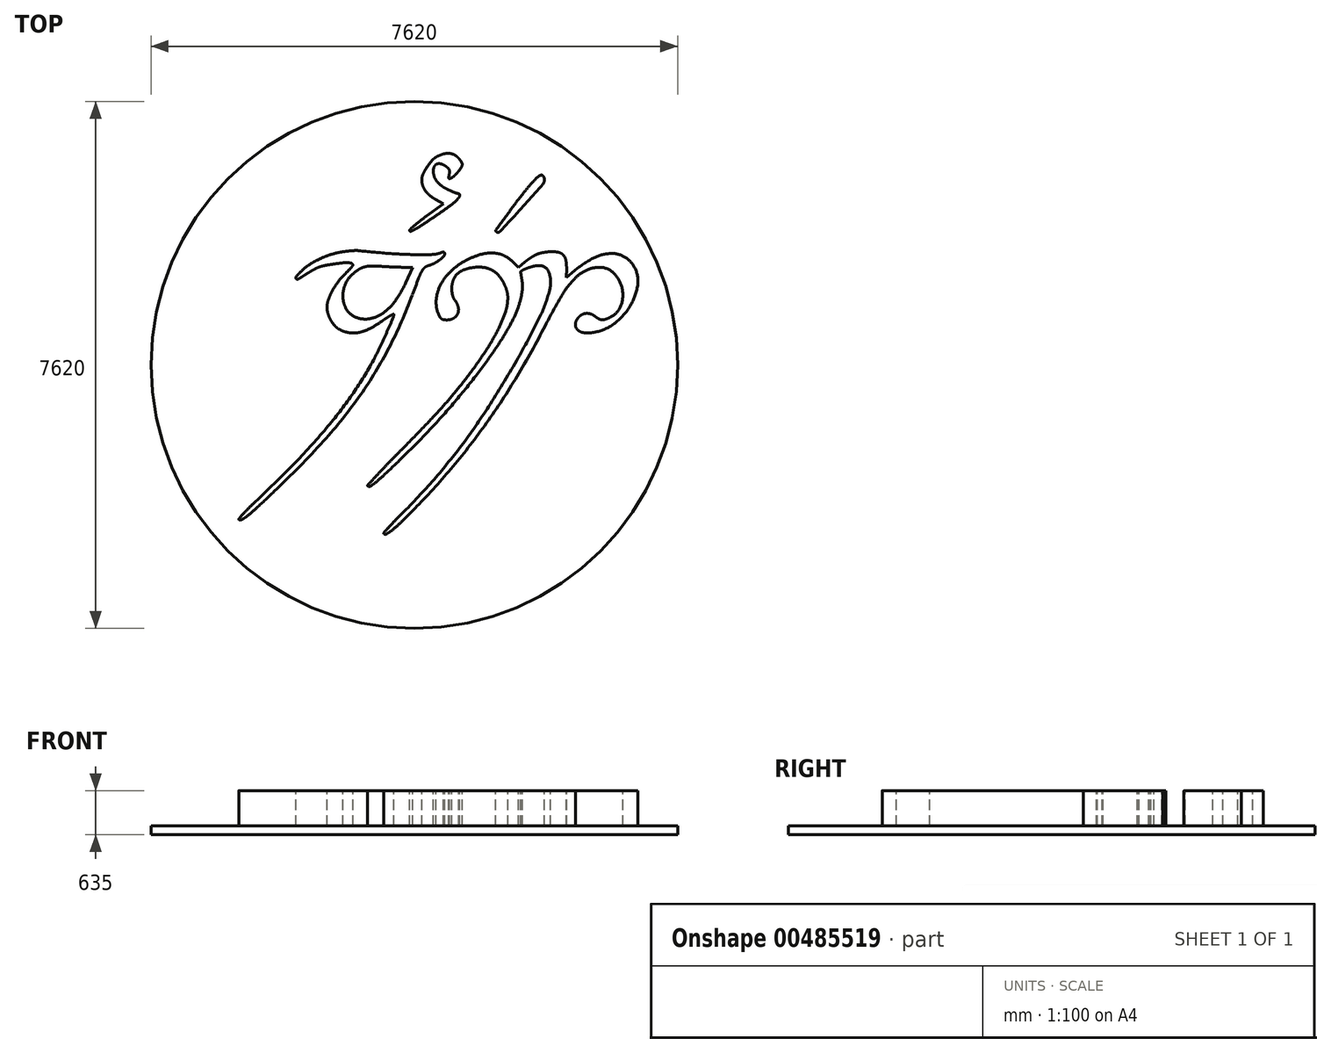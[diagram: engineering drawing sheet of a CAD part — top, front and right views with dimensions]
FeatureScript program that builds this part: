
annotation { "Feature Type Name" : "Feature", "Feature Type Description" : "" }
export const myFeature = defineFeature(function(context is Context, id is Id, definition is map)
    precondition{}
    {
        {
            var Q0;
            Q0=qCreatedBy(makeId("Top.planeOp"),FACE);
            var sketch = newSketch(context, id + "F0", { "sketchPlane" : qUnion([Q0])});
            skCircle(sketch, "E0", {"center": v(-347.42, -304.6) * mm, "radius": 3810 * mm});
            skSolve(sketch);
        }
        {
            var Q0;
            Q0=makeQuery(id+"F0.imprint","IMPRINT",FACE,{"disambiguationData":[TD([[makeQuery(id+"F0.imprint","IMPRINT",EDGE,{"derivedFrom":sQuery(id+"F0.wireOp",EDGE,"E0")}),1.0]])]});
            extrude(context, id + "F1", {"entities" : qUnion([Q0]), "depth" : 635 * mm});
        }
        {
            var Q0;
            Q0=makeQuery(id+"F1.opExtrude","CAP_FACE",FACE,{"disambiguationData":[OSD([sQuery(id+"F0.wireOp",EDGE,"E0")])],"isStart":false});
            var sketch = newSketch(context, id + "F2", { "sketchPlane" : qUnion([Q0])});
            skArc(sketch, "E1", {"start": v(-7.42, 2714.2) * mm, "mid": v(-48.53, 2689.23) * mm, "end": v(-84.64, 2657.45) * mm});
            skArc(sketch, "E2", {"start": v(-84.64, 2657.45) * mm, "mid": v(-125.21, 2611.05) * mm, "end": v(-161.69, 2561.37) * mm});
            skArc(sketch, "E3", {"start": v(-161.69, 2561.37) * mm, "mid": v(-193.23, 2509.73) * mm, "end": v(-220.26, 2455.6) * mm});
            skArc(sketch, "E4", {"start": v(-220.26, 2455.6) * mm, "mid": v(-234, 2413.5) * mm, "end": v(-238.66, 2369.44) * mm});
            skArc(sketch, "E5", {"start": v(-238.66, 2369.44) * mm, "mid": v(-235.35, 2329.08) * mm, "end": v(-225.53, 2289.8) * mm});
            skArc(sketch, "E6", {"start": v(-225.53, 2289.8) * mm, "mid": v(-209.14, 2250.91) * mm, "end": v(-187.32, 2214.8) * mm});
            skArc(sketch, "E7", {"start": v(-187.32, 2214.8) * mm, "mid": v(-158.36, 2179.04) * mm, "end": v(-125, 2147.33) * mm});
            skArc(sketch, "E8", {"start": v(-125, 2147.33) * mm, "mid": v(-84.35, 2116.63) * mm, "end": v(-40.94, 2089.97) * mm});
            skLineSegment(sketch, "E9", {"start": v(-40.94, 2089.97) * mm, "end": v(71.82, 2027.96) * mm});
            skLineSegment(sketch, "E10", {"start": v(71.82, 2027.96) * mm, "end": v(-172.32, 1846.85) * mm});
            skArc(sketch, "E11", {"start": v(-172.32, 1846.85) * mm, "mid": v(-219.33, 1811.5) * mm, "end": v(-265.89, 1775.55) * mm});
            skArc(sketch, "E12", {"start": v(-265.89, 1775.55) * mm, "mid": v(-305.63, 1743.8) * mm, "end": v(-344.74, 1711.28) * mm});
            skArc(sketch, "E13", {"start": v(-344.74, 1711.28) * mm, "mid": v(-377.18, 1683.48) * mm, "end": v(-409.36, 1655.37) * mm});
            skArc(sketch, "E14", {"start": v(-409.36, 1655.37) * mm, "mid": v(-414.6, 1648.27) * mm, "end": v(-416.46, 1639.65) * mm});
            skArc(sketch, "E15", {"start": v(-416.46, 1639.65) * mm, "mid": v(-410.61, 1628.75) * mm, "end": v(-398.3, 1627.6) * mm});
            skArc(sketch, "E16", {"start": v(-398.3, 1627.6) * mm, "mid": v(-361.58, 1644.42) * mm, "end": v(-325.94, 1663.42) * mm});
            skArc(sketch, "E17", {"start": v(-325.94, 1663.42) * mm, "mid": v(-264.04, 1700.28) * mm, "end": v(-203.42, 1739.21) * mm});
            skArc(sketch, "E18", {"start": v(-203.42, 1739.21) * mm, "mid": v(-93.88, 1812.7) * mm, "end": v(15.2, 1886.89) * mm});
            skArc(sketch, "E19", {"start": v(15.2, 1886.89) * mm, "mid": v(101.6, 1947.47) * mm, "end": v(186.62, 2009.96) * mm});
            skArc(sketch, "E20", {"start": v(186.62, 2009.96) * mm, "mid": v(238.22, 2052.19) * mm, "end": v(286.2, 2098.5) * mm});
            skArc(sketch, "E21", {"start": v(286.2, 2098.5) * mm, "mid": v(302.27, 2121.56) * mm, "end": v(310.64, 2148.4) * mm});
            skArc(sketch, "E22", {"start": v(310.64, 2148.4) * mm, "mid": v(305.55, 2166) * mm, "end": v(288.9, 2173.65) * mm});
            skArc(sketch, "E23", {"start": v(288.9, 2173.65) * mm, "mid": v(278.46, 2174.51) * mm, "end": v(268.31, 2177.09) * mm});
            skArc(sketch, "E24", {"start": v(268.31, 2177.09) * mm, "mid": v(247.13, 2184.63) * mm, "end": v(226.12, 2192.62) * mm});
            skArc(sketch, "E25", {"start": v(226.12, 2192.62) * mm, "mid": v(201.18, 2202.76) * mm, "end": v(176.5, 2213.5) * mm});
            skArc(sketch, "E26", {"start": v(176.5, 2213.5) * mm, "mid": v(150.28, 2225.6) * mm, "end": v(124.3, 2238.23) * mm});
            skArc(sketch, "E27", {"start": v(124.3, 2238.23) * mm, "mid": v(75.75, 2265.76) * mm, "end": v(30.4, 2298.31) * mm});
            skArc(sketch, "E28", {"start": v(30.4, 2298.31) * mm, "mid": v(-5.07, 2331.74) * mm, "end": v(-34.77, 2370.4) * mm});
            skArc(sketch, "E29", {"start": v(-34.77, 2370.4) * mm, "mid": v(-55.06, 2409.08) * mm, "end": v(-67.9, 2450.84) * mm});
            skArc(sketch, "E30", {"start": v(-67.9, 2450.84) * mm, "mid": v(-72.44, 2493.19) * mm, "end": v(-68.5, 2535.6) * mm});
            skArc(sketch, "E31", {"start": v(-68.5, 2535.6) * mm, "mid": v(-60.3, 2560.47) * mm, "end": v(-46.08, 2582.47) * mm});
            skArc(sketch, "E32", {"start": v(-46.08, 2582.47) * mm, "mid": v(-28.14, 2597.32) * mm, "end": v(-6.14, 2604.96) * mm});
            skArc(sketch, "E33", {"start": v(-6.14, 2604.96) * mm, "mid": v(21.82, 2605.6) * mm, "end": v(48.99, 2598.91) * mm});
            skArc(sketch, "E34", {"start": v(48.99, 2598.91) * mm, "mid": v(82.44, 2583.45) * mm, "end": v(113.82, 2564.13) * mm});
            skArc(sketch, "E35", {"start": v(113.82, 2564.13) * mm, "mid": v(128.7, 2552.68) * mm, "end": v(142.46, 2539.93) * mm});
            skArc(sketch, "E36", {"start": v(142.46, 2539.93) * mm, "mid": v(151.33, 2528.86) * mm, "end": v(157.76, 2516.22) * mm});
            skArc(sketch, "E37", {"start": v(157.76, 2516.22) * mm, "mid": v(161.57, 2502.33) * mm, "end": v(162.55, 2487.95) * mm});
            skArc(sketch, "E38", {"start": v(162.55, 2487.95) * mm, "mid": v(161.12, 2468.49) * mm, "end": v(158.09, 2449.21) * mm});
            skArc(sketch, "E39", {"start": v(158.09, 2449.21) * mm, "mid": v(153.99, 2427.45) * mm, "end": v(150.38, 2405.6) * mm});
            skArc(sketch, "E40", {"start": v(150.38, 2405.6) * mm, "mid": v(150.66, 2398.38) * mm, "end": v(153.62, 2391.78) * mm});
            skArc(sketch, "E41", {"start": v(153.62, 2391.78) * mm, "mid": v(158.3, 2388.4) * mm, "end": v(164.08, 2388.66) * mm});
            skArc(sketch, "E42", {"start": v(164.08, 2388.66) * mm, "mid": v(178.07, 2394.67) * mm, "end": v(191.69, 2401.47) * mm});
            skArc(sketch, "E43", {"start": v(191.69, 2401.47) * mm, "mid": v(217.15, 2417.49) * mm, "end": v(240.13, 2436.92) * mm});
            skArc(sketch, "E44", {"start": v(240.13, 2436.92) * mm, "mid": v(267.04, 2464.92) * mm, "end": v(292.03, 2494.65) * mm});
            skArc(sketch, "E45", {"start": v(292.03, 2494.65) * mm, "mid": v(313.95, 2524.42) * mm, "end": v(333.95, 2555.5) * mm});
            skArc(sketch, "E46", {"start": v(333.95, 2555.5) * mm, "mid": v(342.6, 2575.63) * mm, "end": v(345.54, 2597.33) * mm});
            skArc(sketch, "E47", {"start": v(345.54, 2597.33) * mm, "mid": v(344.52, 2606.5) * mm, "end": v(341.48, 2615.22) * mm});
            skArc(sketch, "E48", {"start": v(341.48, 2615.22) * mm, "mid": v(334.74, 2628.3) * mm, "end": v(327.23, 2640.94) * mm});
            skArc(sketch, "E49", {"start": v(327.23, 2640.94) * mm, "mid": v(317.55, 2655.26) * mm, "end": v(307.06, 2669) * mm});
            skArc(sketch, "E50", {"start": v(307.06, 2669) * mm, "mid": v(295.48, 2682.56) * mm, "end": v(283.2, 2695.5) * mm});
            skArc(sketch, "E51", {"start": v(283.2, 2695.5) * mm, "mid": v(255.36, 2718.98) * mm, "end": v(223.96, 2737.42) * mm});
            skArc(sketch, "E52", {"start": v(223.96, 2737.42) * mm, "mid": v(191.1, 2749.44) * mm, "end": v(156.55, 2755) * mm});
            skArc(sketch, "E53", {"start": v(156.55, 2755) * mm, "mid": v(117.82, 2754.3) * mm, "end": v(79.72, 2747.2) * mm});
            skArc(sketch, "E54", {"start": v(79.72, 2747.2) * mm, "mid": v(35.36, 2732.79) * mm, "end": v(-7.42, 2714.2) * mm});
            skArc(sketch, "E55", {"start": v(1371.66, 2345.9) * mm, "mid": v(1298.17, 2262.34) * mm, "end": v(1227.93, 2176.04) * mm});
            skArc(sketch, "E56", {"start": v(1227.93, 2176.04) * mm, "mid": v(1131.1, 2050.51) * mm, "end": v(1036, 1923.67) * mm});
            skArc(sketch, "E57", {"start": v(1036, 1923.67) * mm, "mid": v(935.34, 1787.07) * mm, "end": v(835.07, 1650.19) * mm});
            skArc(sketch, "E58", {"start": v(835.07, 1650.19) * mm, "mid": v(831.06, 1636.06) * mm, "end": v(837.2, 1622.73) * mm});
            skArc(sketch, "E59", {"start": v(837.2, 1622.73) * mm, "mid": v(864.38, 1611.72) * mm, "end": v(891.2, 1623.6) * mm});
            skArc(sketch, "E60", {"start": v(891.2, 1623.6) * mm, "mid": v(1048.51, 1792.64) * mm, "end": v(1204.62, 1962.8) * mm});
            skArc(sketch, "E61", {"start": v(1204.62, 1962.8) * mm, "mid": v(1357.47, 2132.12) * mm, "end": v(1508.8, 2302.8) * mm});
            skArc(sketch, "E62", {"start": v(1508.8, 2302.8) * mm, "mid": v(1530.64, 2342.42) * mm, "end": v(1533.83, 2387.56) * mm});
            skArc(sketch, "E63", {"start": v(1533.83, 2387.56) * mm, "mid": v(1527.77, 2409.67) * mm, "end": v(1516.58, 2429.68) * mm});
            skArc(sketch, "E64", {"start": v(1516.58, 2429.68) * mm, "mid": v(1503.37, 2439.56) * mm, "end": v(1486.88, 2440.32) * mm});
            skArc(sketch, "E65", {"start": v(1486.88, 2440.32) * mm, "mid": v(1462.47, 2430.74) * mm, "end": v(1441.12, 2415.5) * mm});
            skArc(sketch, "E66", {"start": v(1441.12, 2415.5) * mm, "mid": v(1405.63, 2381.45) * mm, "end": v(1371.66, 2345.9) * mm});
            skArc(sketch, "E67", {"start": v(-1423.55, 1323.85) * mm, "mid": v(-1503.25, 1306.02) * mm, "end": v(-1581.39, 1282.22) * mm});
            skArc(sketch, "E68", {"start": v(-1581.39, 1282.22) * mm, "mid": v(-1662.29, 1251.3) * mm, "end": v(-1741.07, 1215.33) * mm});
            skArc(sketch, "E69", {"start": v(-1741.07, 1215.33) * mm, "mid": v(-1814.13, 1176.12) * mm, "end": v(-1884.48, 1132.23) * mm});
            skArc(sketch, "E70", {"start": v(-1884.48, 1132.23) * mm, "mid": v(-1940.95, 1089.92) * mm, "end": v(-1992.66, 1041.9) * mm});
            skArc(sketch, "E71", {"start": v(-1992.66, 1041.9) * mm, "mid": v(-2025.38, 1006.75) * mm, "end": v(-2056.66, 970.3) * mm});
            skArc(sketch, "E72", {"start": v(-2056.66, 970.3) * mm, "mid": v(-2061.93, 955.82) * mm, "end": v(-2056.91, 941.26) * mm});
            skArc(sketch, "E73", {"start": v(-2056.91, 941.26) * mm, "mid": v(-2043.96, 933.35) * mm, "end": v(-2028.95, 935.65) * mm});
            skArc(sketch, "E74", {"start": v(-2028.95, 935.65) * mm, "mid": v(-1987.63, 959.45) * mm, "end": v(-1947.32, 984.94) * mm});
            skArc(sketch, "E75", {"start": v(-1947.32, 984.94) * mm, "mid": v(-1926.08, 998.77) * mm, "end": v(-1904.64, 1012.3) * mm});
            skArc(sketch, "E76", {"start": v(-1904.64, 1012.3) * mm, "mid": v(-1880.12, 1027.35) * mm, "end": v(-1855.46, 1042.18) * mm});
            skArc(sketch, "E77", {"start": v(-1855.46, 1042.18) * mm, "mid": v(-1831.55, 1056.23) * mm, "end": v(-1807.5, 1070.04) * mm});
            skArc(sketch, "E78", {"start": v(-1807.5, 1070.04) * mm, "mid": v(-1788.4, 1080.65) * mm, "end": v(-1769.08, 1090.87) * mm});
            skArc(sketch, "E79", {"start": v(-1769.08, 1090.87) * mm, "mid": v(-1722.8, 1111.04) * mm, "end": v(-1674.27, 1124.95) * mm});
            skArc(sketch, "E80", {"start": v(-1674.27, 1124.95) * mm, "mid": v(-1593.1, 1141.17) * mm, "end": v(-1511.43, 1154.72) * mm});
            skArc(sketch, "E81", {"start": v(-1511.43, 1154.72) * mm, "mid": v(-1429.93, 1165.62) * mm, "end": v(-1348.13, 1174.04) * mm});
            skArc(sketch, "E82", {"start": v(-1348.13, 1174.04) * mm, "mid": v(-1304.3, 1174.1) * mm, "end": v(-1261.08, 1166.69) * mm});
            skArc(sketch, "E83", {"start": v(-1261.08, 1166.69) * mm, "mid": v(-1249.45, 1161.4) * mm, "end": v(-1240.27, 1152.5) * mm});
            skArc(sketch, "E84", {"start": v(-1240.27, 1152.5) * mm, "mid": v(-1236.7, 1142.54) * mm, "end": v(-1239.09, 1132.23) * mm});
            skArc(sketch, "E85", {"start": v(-1239.09, 1132.23) * mm, "mid": v(-1251.3, 1113.44) * mm, "end": v(-1265.76, 1096.33) * mm});
            skArc(sketch, "E86", {"start": v(-1265.76, 1096.33) * mm, "mid": v(-1306.73, 1054.1) * mm, "end": v(-1348.12, 1012.28) * mm});
            skArc(sketch, "E87", {"start": v(-1348.12, 1012.28) * mm, "mid": v(-1402.48, 954) * mm, "end": v(-1452.66, 892.1) * mm});
            skArc(sketch, "E88", {"start": v(-1452.66, 892.1) * mm, "mid": v(-1497, 828.5) * mm, "end": v(-1536.43, 761.73) * mm});
            skArc(sketch, "E89", {"start": v(-1536.43, 761.73) * mm, "mid": v(-1566.77, 699.66) * mm, "end": v(-1591.9, 635.3) * mm});
            skArc(sketch, "E90", {"start": v(-1591.9, 635.3) * mm, "mid": v(-1605.37, 582.4) * mm, "end": v(-1610, 527.98) * mm});
            skArc(sketch, "E91", {"start": v(-1610, 527.98) * mm, "mid": v(-1606.88, 483.87) * mm, "end": v(-1597.3, 440.7) * mm});
            skArc(sketch, "E92", {"start": v(-1597.3, 440.7) * mm, "mid": v(-1580.42, 393.36) * mm, "end": v(-1558.86, 347.96) * mm});
            skArc(sketch, "E93", {"start": v(-1558.86, 347.96) * mm, "mid": v(-1533.4, 305.96) * mm, "end": v(-1503.77, 266.78) * mm});
            skArc(sketch, "E94", {"start": v(-1503.77, 266.78) * mm, "mid": v(-1474.8, 237.85) * mm, "end": v(-1441.22, 214.43) * mm});
            skArc(sketch, "E95", {"start": v(-1441.22, 214.43) * mm, "mid": v(-1373.22, 182.62) * mm, "end": v(-1300.86, 162.6) * mm});
            skArc(sketch, "E96", {"start": v(-1300.86, 162.6) * mm, "mid": v(-1228.43, 155.78) * mm, "end": v(-1155.98, 162.35) * mm});
            skArc(sketch, "E97", {"start": v(-1155.98, 162.35) * mm, "mid": v(-1074.18, 183.8) * mm, "end": v(-996.45, 217.1) * mm});
            skArc(sketch, "E98", {"start": v(-996.45, 217.1) * mm, "mid": v(-901.61, 270.65) * mm, "end": v(-810.78, 330.76) * mm});
            skArc(sketch, "E99", {"start": v(-810.78, 330.76) * mm, "mid": v(-779.18, 352.87) * mm, "end": v(-747.19, 374.4) * mm});
            skArc(sketch, "E100", {"start": v(-747.19, 374.4) * mm, "mid": v(-720.74, 391.2) * mm, "end": v(-693.74, 407.1) * mm});
            skArc(sketch, "E101", {"start": v(-693.74, 407.1) * mm, "mid": v(-673.16, 418.37) * mm, "end": v(-652.29, 429.07) * mm});
            skArc(sketch, "E102", {"start": v(-652.29, 429.07) * mm, "mid": v(-647.42, 428.84) * mm, "end": v(-645.06, 424.58) * mm});
            skArc(sketch, "E103", {"start": v(-645.06, 424.58) * mm, "mid": v(-647.82, 397.46) * mm, "end": v(-656, 371.45) * mm});
            skArc(sketch, "E104", {"start": v(-656, 371.45) * mm, "mid": v(-701.59, 266.29) * mm, "end": v(-747.81, 161.4) * mm});
            skArc(sketch, "E105", {"start": v(-747.81, 161.4) * mm, "mid": v(-796.53, 53.71) * mm, "end": v(-846.7, -53.31) * mm});
            skArc(sketch, "E106", {"start": v(-846.7, -53.31) * mm, "mid": v(-891.15, -144) * mm, "end": v(-937.54, -233.7) * mm});
            skArc(sketch, "E107", {"start": v(-937.54, -233.7) * mm, "mid": v(-1075.1, -475.43) * mm, "end": v(-1226.62, -708.66) * mm});
            skArc(sketch, "E108", {"start": v(-1226.62, -708.66) * mm, "mid": v(-1404.23, -953.06) * mm, "end": v(-1592.86, -1189.06) * mm});
            skArc(sketch, "E109", {"start": v(-1592.86, -1189.06) * mm, "mid": v(-1824.72, -1455.4) * mm, "end": v(-2066.57, -1712.72) * mm});
            skArc(sketch, "E110", {"start": v(-2066.57, -1712.72) * mm, "mid": v(-2373.68, -2020.83) * mm, "end": v(-2687.06, -2322.55) * mm});
            skArc(sketch, "E111", {"start": v(-2687.06, -2322.55) * mm, "mid": v(-2729.67, -2363.42) * mm, "end": v(-2771.59, -2405) * mm});
            skArc(sketch, "E112", {"start": v(-2771.59, -2405) * mm, "mid": v(-2805.24, -2439.98) * mm, "end": v(-2837.83, -2475.95) * mm});
            skArc(sketch, "E113", {"start": v(-2837.83, -2475.95) * mm, "mid": v(-2862.5, -2504.58) * mm, "end": v(-2886.57, -2533.69) * mm});
            skArc(sketch, "E114", {"start": v(-2886.57, -2533.69) * mm, "mid": v(-2887.94, -2540.54) * mm, "end": v(-2883.1, -2545.57) * mm});
            skArc(sketch, "E115", {"start": v(-2883.1, -2545.57) * mm, "mid": v(-2858.86, -2548.1) * mm, "end": v(-2835.82, -2540.19) * mm});
            skArc(sketch, "E116", {"start": v(-2835.82, -2540.19) * mm, "mid": v(-2794.43, -2513) * mm, "end": v(-2754.89, -2483.2) * mm});
            skArc(sketch, "E117", {"start": v(-2754.89, -2483.2) * mm, "mid": v(-2689.5, -2428.58) * mm, "end": v(-2626.05, -2371.68) * mm});
            skArc(sketch, "E118", {"start": v(-2626.05, -2371.68) * mm, "mid": v(-2500.37, -2254.32) * mm, "end": v(-2375.3, -2136.31) * mm});
            skArc(sketch, "E119", {"start": v(-2375.3, -2136.31) * mm, "mid": v(-2011, -1777.76) * mm, "end": v(-1660.16, -1406.02) * mm});
            skArc(sketch, "E120", {"start": v(-1660.16, -1406.02) * mm, "mid": v(-1382.35, -1080.67) * mm, "end": v(-1125.43, -738.59) * mm});
            skArc(sketch, "E121", {"start": v(-1125.43, -738.59) * mm, "mid": v(-908, -405.57) * mm, "end": v(-713.98, -58.39) * mm});
            skArc(sketch, "E122", {"start": v(-713.98, -58.39) * mm, "mid": v(-533.5, 319.48) * mm, "end": v(-375.6, 707.33) * mm});
            skArc(sketch, "E123", {"start": v(-375.6, 707.33) * mm, "mid": v(-328.27, 833.1) * mm, "end": v(-280.22, 958.58) * mm});
            skArc(sketch, "E124", {"start": v(-280.22, 958.58) * mm, "mid": v(-259.53, 1007.3) * mm, "end": v(-235.69, 1054.54) * mm});
            skArc(sketch, "E125", {"start": v(-235.69, 1054.54) * mm, "mid": v(-218.19, 1080.58) * mm, "end": v(-196.24, 1103) * mm});
            skArc(sketch, "E126", {"start": v(-196.24, 1103) * mm, "mid": v(-171.74, 1119.6) * mm, "end": v(-144.23, 1130.53) * mm});
            skArc(sketch, "E127", {"start": v(-144.23, 1130.53) * mm, "mid": v(-103.31, 1144.02) * mm, "end": v(-63.9, 1161.44) * mm});
            skArc(sketch, "E128", {"start": v(-63.9, 1161.44) * mm, "mid": v(-23.81, 1183.67) * mm, "end": v(14.34, 1209.08) * mm});
            skArc(sketch, "E129", {"start": v(14.34, 1209.08) * mm, "mid": v(45.6, 1233.77) * mm, "end": v(74.74, 1260.92) * mm});
            skArc(sketch, "E130", {"start": v(74.74, 1260.92) * mm, "mid": v(87.18, 1279.7) * mm, "end": v(91.54, 1301.8) * mm});
            skArc(sketch, "E131", {"start": v(91.54, 1301.8) * mm, "mid": v(90.89, 1310.25) * mm, "end": v(88.93, 1318.51) * mm});
            skArc(sketch, "E132", {"start": v(88.93, 1318.51) * mm, "mid": v(85.96, 1323.68) * mm, "end": v(81.14, 1327.17) * mm});
            skArc(sketch, "E133", {"start": v(81.14, 1327.17) * mm, "mid": v(74.53, 1328.87) * mm, "end": v(67.72, 1328.36) * mm});
            skArc(sketch, "E134", {"start": v(67.72, 1328.36) * mm, "mid": v(57.26, 1325.34) * mm, "end": v(47.1, 1321.4) * mm});
            skArc(sketch, "E135", {"start": v(47.1, 1321.4) * mm, "mid": v(-17.12, 1300.34) * mm, "end": v(-84.18, 1291.92) * mm});
            skArc(sketch, "E136", {"start": v(-84.18, 1291.92) * mm, "mid": v(-227.66, 1289.6) * mm, "end": v(-371.15, 1290.9) * mm});
            skArc(sketch, "E137", {"start": v(-371.15, 1290.9) * mm, "mid": v(-551.78, 1297.28) * mm, "end": v(-732.18, 1308.51) * mm});
            skArc(sketch, "E138", {"start": v(-732.18, 1308.51) * mm, "mid": v(-942.78, 1326.27) * mm, "end": v(-1153.06, 1347.59) * mm});
            skArc(sketch, "E139", {"start": v(-1153.06, 1347.59) * mm, "mid": v(-1176.14, 1349.24) * mm, "end": v(-1199.29, 1349.16) * mm});
            skArc(sketch, "E140", {"start": v(-1199.29, 1349.16) * mm, "mid": v(-1234.26, 1347.3) * mm, "end": v(-1269.18, 1344.64) * mm});
            skArc(sketch, "E141", {"start": v(-1269.18, 1344.64) * mm, "mid": v(-1308.4, 1340.75) * mm, "end": v(-1347.5, 1335.96) * mm});
            skArc(sketch, "E142", {"start": v(-1347.5, 1335.96) * mm, "mid": v(-1385.6, 1330.37) * mm, "end": v(-1423.55, 1323.85) * mm});
            skLineSegment(sketch, "E143", {"start": v(-500.17, 1107) * mm, "end": v(-367.98, 1106.85) * mm});
            skLineSegment(sketch, "E144", {"start": v(-367.98, 1106.85) * mm, "end": v(-469.87, 884.6) * mm});
            skArc(sketch, "E145", {"start": v(-469.87, 884.6) * mm, "mid": v(-546.84, 737.86) * mm, "end": v(-638.97, 600.14) * mm});
            skArc(sketch, "E146", {"start": v(-638.97, 600.14) * mm, "mid": v(-730.37, 499.78) * mm, "end": v(-839.22, 418.68) * mm});
            skArc(sketch, "E147", {"start": v(-839.22, 418.68) * mm, "mid": v(-939.85, 374.38) * mm, "end": v(-1048.5, 357.42) * mm});
            skArc(sketch, "E148", {"start": v(-1048.5, 357.42) * mm, "mid": v(-1152.04, 370.57) * mm, "end": v(-1246.97, 413.97) * mm});
            skArc(sketch, "E149", {"start": v(-1246.97, 413.97) * mm, "mid": v(-1303.62, 463.73) * mm, "end": v(-1344.22, 527.27) * mm});
            skArc(sketch, "E150", {"start": v(-1344.22, 527.27) * mm, "mid": v(-1370.65, 606.27) * mm, "end": v(-1380.04, 689.05) * mm});
            skArc(sketch, "E151", {"start": v(-1380.04, 689.05) * mm, "mid": v(-1372.1, 776.04) * mm, "end": v(-1347.22, 859.76) * mm});
            skArc(sketch, "E152", {"start": v(-1347.22, 859.76) * mm, "mid": v(-1307, 933.77) * mm, "end": v(-1251.58, 997.2) * mm});
            skArc(sketch, "E153", {"start": v(-1251.58, 997.2) * mm, "mid": v(-1206.84, 1035.32) * mm, "end": v(-1159.4, 1070.01) * mm});
            skArc(sketch, "E154", {"start": v(-1159.4, 1070.01) * mm, "mid": v(-1119.42, 1092.8) * mm, "end": v(-1076.46, 1109.28) * mm});
            skArc(sketch, "E155", {"start": v(-1076.46, 1109.28) * mm, "mid": v(-1028.06, 1120.27) * mm, "end": v(-978.62, 1124.72) * mm});
            skArc(sketch, "E156", {"start": v(-978.62, 1124.72) * mm, "mid": v(-907.05, 1124.7) * mm, "end": v(-835.56, 1121.37) * mm});
            skArc(sketch, "E157", {"start": v(-835.56, 1121.37) * mm, "mid": v(-791.83, 1118.48) * mm, "end": v(-748.08, 1115.91) * mm});
            skArc(sketch, "E158", {"start": v(-748.08, 1115.91) * mm, "mid": v(-700.65, 1113.46) * mm, "end": v(-653.22, 1111.28) * mm});
            skArc(sketch, "E159", {"start": v(-653.22, 1111.28) * mm, "mid": v(-609.1, 1109.53) * mm, "end": v(-564.98, 1108.03) * mm});
            skArc(sketch, "E160", {"start": v(-564.98, 1108.03) * mm, "mid": v(-532.58, 1107.28) * mm, "end": v(-500.17, 1107) * mm});
            skArc(sketch, "E161", {"start": v(1441.23, 1300.67) * mm, "mid": v(1421.03, 1292.53) * mm, "end": v(1401.47, 1282.97) * mm});
            skArc(sketch, "E162", {"start": v(1401.47, 1282.97) * mm, "mid": v(1376.36, 1269.05) * mm, "end": v(1351.7, 1254.33) * mm});
            skArc(sketch, "E163", {"start": v(1351.7, 1254.33) * mm, "mid": v(1325.95, 1237.83) * mm, "end": v(1300.73, 1220.53) * mm});
            skArc(sketch, "E164", {"start": v(1300.73, 1220.53) * mm, "mid": v(1278.22, 1203.88) * mm, "end": v(1256.42, 1186.32) * mm});
            skLineSegment(sketch, "E165", {"start": v(1256.42, 1186.32) * mm, "end": v(1157.03, 1102.88) * mm});
            skLineSegment(sketch, "E166", {"start": v(1157.03, 1102.88) * mm, "end": v(1084.47, 1180.56) * mm});
            skArc(sketch, "E167", {"start": v(1084.47, 1180.56) * mm, "mid": v(1024.7, 1233.4) * mm, "end": v(955.97, 1273.94) * mm});
            skArc(sketch, "E168", {"start": v(955.97, 1273.94) * mm, "mid": v(880.54, 1300.88) * mm, "end": v(801.4, 1313.18) * mm});
            skArc(sketch, "E169", {"start": v(801.4, 1313.18) * mm, "mid": v(711.63, 1311.29) * mm, "end": v(623.33, 1294.96) * mm});
            skArc(sketch, "E170", {"start": v(623.33, 1294.96) * mm, "mid": v(522.9, 1262.39) * mm, "end": v(426.25, 1219.94) * mm});
            skArc(sketch, "E171", {"start": v(426.25, 1219.94) * mm, "mid": v(305.83, 1149.2) * mm, "end": v(195.97, 1062.97) * mm});
            skArc(sketch, "E172", {"start": v(195.97, 1062.97) * mm, "mid": v(108.04, 969.03) * mm, "end": v(37.44, 861.46) * mm});
            skArc(sketch, "E173", {"start": v(37.44, 861.46) * mm, "mid": v(-7.04, 755.18) * mm, "end": v(-29.8, 642.25) * mm});
            skArc(sketch, "E174", {"start": v(-29.8, 642.25) * mm, "mid": v(-27.28, 535.65) * mm, "end": v(1.35, 432.93) * mm});
            skArc(sketch, "E175", {"start": v(1.35, 432.93) * mm, "mid": v(12.32, 408.68) * mm, "end": v(24.7, 385.12) * mm});
            skArc(sketch, "E176", {"start": v(24.7, 385.12) * mm, "mid": v(34.43, 371.54) * mm, "end": v(46.88, 360.39) * mm});
            skArc(sketch, "E177", {"start": v(46.88, 360.39) * mm, "mid": v(60.94, 352.65) * mm, "end": v(76.43, 348.42) * mm});
            skArc(sketch, "E178", {"start": v(76.43, 348.42) * mm, "mid": v(100.35, 345.74) * mm, "end": v(124.41, 344.85) * mm});
            skArc(sketch, "E179", {"start": v(124.41, 344.85) * mm, "mid": v(174.18, 351.1) * mm, "end": v(220.85, 369.5) * mm});
            skArc(sketch, "E180", {"start": v(220.85, 369.5) * mm, "mid": v(256.58, 397.62) * mm, "end": v(281.14, 435.88) * mm});
            skArc(sketch, "E181", {"start": v(281.14, 435.88) * mm, "mid": v(292.66, 481.57) * mm, "end": v(289.48, 528.58) * mm});
            skArc(sketch, "E182", {"start": v(289.48, 528.58) * mm, "mid": v(271.98, 578.92) * mm, "end": v(243.94, 624.25) * mm});
            skArc(sketch, "E183", {"start": v(243.94, 624.25) * mm, "mid": v(223.5, 656.24) * mm, "end": v(209.52, 691.53) * mm});
            skArc(sketch, "E184", {"start": v(209.52, 691.53) * mm, "mid": v(199.73, 734.86) * mm, "end": v(195.2, 779.04) * mm});
            skArc(sketch, "E185", {"start": v(195.2, 779.04) * mm, "mid": v(195.94, 825.3) * mm, "end": v(202.02, 871.15) * mm});
            skArc(sketch, "E186", {"start": v(202.02, 871.15) * mm, "mid": v(213.15, 912.73) * mm, "end": v(230.13, 952.28) * mm});
            skArc(sketch, "E187", {"start": v(230.13, 952.28) * mm, "mid": v(269.91, 1006.88) * mm, "end": v(324.26, 1047) * mm});
            skArc(sketch, "E188", {"start": v(324.26, 1047) * mm, "mid": v(402.18, 1080.39) * mm, "end": v(484.37, 1101.12) * mm});
            skArc(sketch, "E189", {"start": v(484.37, 1101.12) * mm, "mid": v(572.53, 1109.3) * mm, "end": v(660.92, 1104.12) * mm});
            skArc(sketch, "E190", {"start": v(660.92, 1104.12) * mm, "mid": v(735.33, 1085.15) * mm, "end": v(803.45, 1049.7) * mm});
            skArc(sketch, "E191", {"start": v(803.45, 1049.7) * mm, "mid": v(844.39, 1017.33) * mm, "end": v(880.11, 979.28) * mm});
            skArc(sketch, "E192", {"start": v(880.11, 979.28) * mm, "mid": v(915.4, 930.96) * mm, "end": v(945.78, 879.4) * mm});
            skArc(sketch, "E193", {"start": v(945.78, 879.4) * mm, "mid": v(970.98, 825) * mm, "end": v(990.73, 768.4) * mm});
            skArc(sketch, "E194", {"start": v(990.73, 768.4) * mm, "mid": v(1001.85, 717.09) * mm, "end": v(1005.4, 664.7) * mm});
            skArc(sketch, "E195", {"start": v(1005.4, 664.7) * mm, "mid": v(996.98, 564.7) * mm, "end": v(972.92, 467.29) * mm});
            skArc(sketch, "E196", {"start": v(972.92, 467.29) * mm, "mid": v(926.43, 341.96) * mm, "end": v(871.48, 220.1) * mm});
            skArc(sketch, "E197", {"start": v(871.48, 220.1) * mm, "mid": v(794.46, 74.4) * mm, "end": v(709.29, -66.69) * mm});
            skArc(sketch, "E198", {"start": v(709.29, -66.69) * mm, "mid": v(600.63, -229.46) * mm, "end": v(486.49, -388.43) * mm});
            skArc(sketch, "E199", {"start": v(486.49, -388.43) * mm, "mid": v(384.16, -522.96) * mm, "end": v(279.04, -655.32) * mm});
            skArc(sketch, "E200", {"start": v(279.04, -655.32) * mm, "mid": v(175, -780.52) * mm, "end": v(68.06, -903.25) * mm});
            skArc(sketch, "E201", {"start": v(68.06, -903.25) * mm, "mid": v(-59.8, -1043.87) * mm, "end": v(-190.27, -1182.07) * mm});
            skArc(sketch, "E202", {"start": v(-190.27, -1182.07) * mm, "mid": v(-370.65, -1368.16) * mm, "end": v(-552.44, -1552.87) * mm});
            skArc(sketch, "E203", {"start": v(-552.44, -1552.87) * mm, "mid": v(-644.92, -1646.74) * mm, "end": v(-736.78, -1741.22) * mm});
            skArc(sketch, "E204", {"start": v(-736.78, -1741.22) * mm, "mid": v(-813.44, -1821.46) * mm, "end": v(-889.22, -1902.54) * mm});
            skArc(sketch, "E205", {"start": v(-889.22, -1902.54) * mm, "mid": v(-954.5, -1973.34) * mm, "end": v(-1019.62, -2044.3) * mm});
            skArc(sketch, "E206", {"start": v(-1019.62, -2044.3) * mm, "mid": v(-1022.2, -2051.2) * mm, "end": v(-1019.32, -2057.96) * mm});
            skArc(sketch, "E207", {"start": v(-1019.32, -2057.96) * mm, "mid": v(-1002.99, -2065.77) * mm, "end": v(-985.37, -2061.61) * mm});
            skArc(sketch, "E208", {"start": v(-985.37, -2061.61) * mm, "mid": v(-945.35, -2034.3) * mm, "end": v(-906.93, -2004.8) * mm});
            skArc(sketch, "E209", {"start": v(-906.93, -2004.8) * mm, "mid": v(-843.74, -1951.5) * mm, "end": v(-782.45, -1896.03) * mm});
            skArc(sketch, "E210", {"start": v(-782.45, -1896.03) * mm, "mid": v(-667.9, -1788) * mm, "end": v(-553.98, -1679.29) * mm});
            skArc(sketch, "E211", {"start": v(-553.98, -1679.29) * mm, "mid": v(-347.68, -1476.21) * mm, "end": v(-146.5, -1268.05) * mm});
            skArc(sketch, "E212", {"start": v(-146.5, -1268.05) * mm, "mid": v(48.77, -1055.6) * mm, "end": v(238.62, -838.3) * mm});
            skArc(sketch, "E213", {"start": v(238.62, -838.3) * mm, "mid": v(414.09, -626.72) * mm, "end": v(583.94, -410.61) * mm});
            skArc(sketch, "E214", {"start": v(583.94, -410.61) * mm, "mid": v(731.2, -210.82) * mm, "end": v(871.27, -5.92) * mm});
            skArc(sketch, "E215", {"start": v(871.27, -5.92) * mm, "mid": v(962.08, 138.43) * mm, "end": v(1046.97, 286.32) * mm});
            skArc(sketch, "E216", {"start": v(1046.97, 286.32) * mm, "mid": v(1107.57, 408.2) * mm, "end": v(1158.4, 534.45) * mm});
            skArc(sketch, "E217", {"start": v(1158.4, 534.45) * mm, "mid": v(1190.32, 640.13) * mm, "end": v(1211.5, 748.48) * mm});
            skArc(sketch, "E218", {"start": v(1211.5, 748.48) * mm, "mid": v(1217.3, 842.16) * mm, "end": v(1207.9, 935.55) * mm});
            skArc(sketch, "E219", {"start": v(1207.9, 935.55) * mm, "mid": v(1204.19, 956.31) * mm, "end": v(1200.63, 977.1) * mm});
            skArc(sketch, "E220", {"start": v(1200.63, 977.1) * mm, "mid": v(1197.8, 994.83) * mm, "end": v(1195.17, 1012.6) * mm});
            skArc(sketch, "E221", {"start": v(1195.17, 1012.6) * mm, "mid": v(1193.04, 1027.94) * mm, "end": v(1190.97, 1043.29) * mm});
            skArc(sketch, "E222", {"start": v(1190.97, 1043.29) * mm, "mid": v(1191.2, 1045.06) * mm, "end": v(1192.3, 1046.47) * mm});
            skArc(sketch, "E223", {"start": v(1192.3, 1046.47) * mm, "mid": v(1217.94, 1063.58) * mm, "end": v(1245.35, 1077.69) * mm});
            skArc(sketch, "E224", {"start": v(1245.35, 1077.69) * mm, "mid": v(1281.78, 1092.71) * mm, "end": v(1318.98, 1105.71) * mm});
            skArc(sketch, "E225", {"start": v(1318.98, 1105.71) * mm, "mid": v(1357.36, 1116.8) * mm, "end": v(1396.3, 1125.76) * mm});
            skArc(sketch, "E226", {"start": v(1396.3, 1125.76) * mm, "mid": v(1428.64, 1130.62) * mm, "end": v(1461.3, 1132.25) * mm});
            skArc(sketch, "E227", {"start": v(1461.3, 1132.25) * mm, "mid": v(1546.3, 1105.5) * mm, "end": v(1600.7, 1034.93) * mm});
            skArc(sketch, "E228", {"start": v(1600.7, 1034.93) * mm, "mid": v(1624.91, 920) * mm, "end": v(1615.45, 802.92) * mm});
            skArc(sketch, "E229", {"start": v(1615.45, 802.92) * mm, "mid": v(1555.54, 596.21) * mm, "end": v(1472.4, 397.71) * mm});
            skArc(sketch, "E230", {"start": v(1472.4, 397.71) * mm, "mid": v(1319.1, 95.73) * mm, "end": v(1156.36, -201.25) * mm});
            skArc(sketch, "E231", {"start": v(1156.36, -201.25) * mm, "mid": v(959.17, -537.81) * mm, "end": v(753.37, -869.17) * mm});
            skArc(sketch, "E232", {"start": v(753.37, -869.17) * mm, "mid": v(560.4, -1159.43) * mm, "end": v(357.07, -1442.52) * mm});
            skArc(sketch, "E233", {"start": v(357.07, -1442.52) * mm, "mid": v(153.31, -1705.05) * mm, "end": v(-60.32, -1959.6) * mm});
            skArc(sketch, "E234", {"start": v(-60.32, -1959.6) * mm, "mid": v(-288.96, -2212.5) * mm, "end": v(-526.4, -2457.15) * mm});
            skArc(sketch, "E235", {"start": v(-526.4, -2457.15) * mm, "mid": v(-579.12, -2510.06) * mm, "end": v(-631.36, -2563.45) * mm});
            skArc(sketch, "E236", {"start": v(-631.36, -2563.45) * mm, "mid": v(-674.8, -2608.94) * mm, "end": v(-717.56, -2655.09) * mm});
            skArc(sketch, "E237", {"start": v(-717.56, -2655.09) * mm, "mid": v(-753.64, -2694.82) * mm, "end": v(-789.54, -2734.7) * mm});
            skArc(sketch, "E238", {"start": v(-789.54, -2734.7) * mm, "mid": v(-791.5, -2740.02) * mm, "end": v(-789.25, -2745.22) * mm});
            skArc(sketch, "E239", {"start": v(-789.25, -2745.22) * mm, "mid": v(-768.9, -2755.2) * mm, "end": v(-746.69, -2750.65) * mm});
            skArc(sketch, "E240", {"start": v(-746.69, -2750.65) * mm, "mid": v(-703.02, -2722.62) * mm, "end": v(-661.65, -2691.3) * mm});
            skArc(sketch, "E241", {"start": v(-661.65, -2691.3) * mm, "mid": v(-595.04, -2634.11) * mm, "end": v(-531.1, -2573.95) * mm});
            skArc(sketch, "E242", {"start": v(-531.1, -2573.95) * mm, "mid": v(-420.6, -2464.1) * mm, "end": v(-311.12, -2353.24) * mm});
            skArc(sketch, "E243", {"start": v(-311.12, -2353.24) * mm, "mid": v(-42, -2067.13) * mm, "end": v(215.6, -1770.62) * mm});
            skArc(sketch, "E244", {"start": v(215.6, -1770.62) * mm, "mid": v(462.35, -1463.02) * mm, "end": v(696.9, -1146.03) * mm});
            skArc(sketch, "E245", {"start": v(696.9, -1146.03) * mm, "mid": v(924.16, -812.79) * mm, "end": v(1138.55, -471.13) * mm});
            skArc(sketch, "E246", {"start": v(1138.55, -471.13) * mm, "mid": v(1348.68, -107.88) * mm, "end": v(1546.4, 262.27) * mm});
            skArc(sketch, "E247", {"start": v(1546.4, 262.27) * mm, "mid": v(1661.2, 478.52) * mm, "end": v(1782.11, 691.4) * mm});
            skArc(sketch, "E248", {"start": v(1782.11, 691.4) * mm, "mid": v(1866.16, 818.05) * mm, "end": v(1963.62, 934.68) * mm});
            skArc(sketch, "E249", {"start": v(1963.62, 934.68) * mm, "mid": v(2044.54, 1006.52) * mm, "end": v(2137.4, 1062.06) * mm});
            skArc(sketch, "E250", {"start": v(2137.4, 1062.06) * mm, "mid": v(2233.76, 1095.5) * mm, "end": v(2335.12, 1106.85) * mm});
            skArc(sketch, "E251", {"start": v(2335.12, 1106.85) * mm, "mid": v(2446.23, 1084.66) * mm, "end": v(2540.3, 1021.5) * mm});
            skArc(sketch, "E252", {"start": v(2540.3, 1021.5) * mm, "mid": v(2615.85, 919.85) * mm, "end": v(2659.62, 801) * mm});
            skArc(sketch, "E253", {"start": v(2659.62, 801) * mm, "mid": v(2668.31, 673.74) * mm, "end": v(2641.1, 549.11) * mm});
            skArc(sketch, "E254", {"start": v(2641.1, 549.11) * mm, "mid": v(2581.3, 451.4) * mm, "end": v(2489.12, 383.36) * mm});
            skArc(sketch, "E255", {"start": v(2489.12, 383.36) * mm, "mid": v(2453.78, 367.83) * mm, "end": v(2417.58, 354.4) * mm});
            skArc(sketch, "E256", {"start": v(2417.58, 354.4) * mm, "mid": v(2392.93, 348.65) * mm, "end": v(2367.64, 347.78) * mm});
            skArc(sketch, "E257", {"start": v(2367.64, 347.78) * mm, "mid": v(2344.18, 351.85) * mm, "end": v(2322.15, 360.9) * mm});
            skArc(sketch, "E258", {"start": v(2322.15, 360.9) * mm, "mid": v(2293.73, 377.97) * mm, "end": v(2266.85, 397.35) * mm});
            skArc(sketch, "E259", {"start": v(2266.85, 397.35) * mm, "mid": v(2235.45, 417.94) * mm, "end": v(2200.98, 432.86) * mm});
            skArc(sketch, "E260", {"start": v(2200.98, 432.86) * mm, "mid": v(2167.26, 440.1) * mm, "end": v(2132.77, 439.77) * mm});
            skArc(sketch, "E261", {"start": v(2132.77, 439.77) * mm, "mid": v(2099.55, 431.9) * mm, "end": v(2068.9, 416.83) * mm});
            skArc(sketch, "E262", {"start": v(2068.9, 416.83) * mm, "mid": v(2039.9, 394.32) * mm, "end": v(2015.43, 366.95) * mm});
            skArc(sketch, "E263", {"start": v(2015.43, 366.95) * mm, "mid": v(1992.05, 322.38) * mm, "end": v(1983.48, 272.78) * mm});
            skArc(sketch, "E264", {"start": v(1983.48, 272.78) * mm, "mid": v(1992.95, 230.27) * mm, "end": v(2020.61, 196.62) * mm});
            skArc(sketch, "E265", {"start": v(2020.61, 196.62) * mm, "mid": v(2070.66, 169.27) * mm, "end": v(2126.5, 157.75) * mm});
            skArc(sketch, "E266", {"start": v(2126.5, 157.75) * mm, "mid": v(2201.68, 158.6) * mm, "end": v(2276.07, 169.45) * mm});
            skArc(sketch, "E267", {"start": v(2276.07, 169.45) * mm, "mid": v(2424.22, 219.24) * mm, "end": v(2557.43, 300.96) * mm});
            skArc(sketch, "E268", {"start": v(2557.43, 300.96) * mm, "mid": v(2679.5, 415.84) * mm, "end": v(2778.54, 551.08) * mm});
            skArc(sketch, "E269", {"start": v(2778.54, 551.08) * mm, "mid": v(2845.82, 693.5) * mm, "end": v(2883.8, 846.36) * mm});
            skArc(sketch, "E270", {"start": v(2883.8, 846.36) * mm, "mid": v(2881.98, 980.42) * mm, "end": v(2838.51, 1107.24) * mm});
            skArc(sketch, "E271", {"start": v(2838.51, 1107.24) * mm, "mid": v(2775.8, 1193.36) * mm, "end": v(2691.6, 1258.62) * mm});
            skArc(sketch, "E272", {"start": v(2691.6, 1258.62) * mm, "mid": v(2593.19, 1297.3) * mm, "end": v(2487.83, 1306.41) * mm});
            skArc(sketch, "E273", {"start": v(2487.83, 1306.41) * mm, "mid": v(2360.1, 1285.32) * mm, "end": v(2239.68, 1237.82) * mm});
            skArc(sketch, "E274", {"start": v(2239.68, 1237.82) * mm, "mid": v(2099.86, 1154.78) * mm, "end": v(1969.85, 1057.07) * mm});
            skLineSegment(sketch, "E275", {"start": v(1969.85, 1057.07) * mm, "end": v(1854.26, 959.95) * mm});
            skLineSegment(sketch, "E276", {"start": v(1854.26, 959.95) * mm, "end": v(1855.55, 1094.18) * mm});
            skArc(sketch, "E277", {"start": v(1855.55, 1094.18) * mm, "mid": v(1853.3, 1152.47) * mm, "end": v(1845.45, 1210.27) * mm});
            skArc(sketch, "E278", {"start": v(1845.45, 1210.27) * mm, "mid": v(1832.7, 1248.9) * mm, "end": v(1810.07, 1282.72) * mm});
            skArc(sketch, "E279", {"start": v(1810.07, 1282.72) * mm, "mid": v(1780.61, 1307.27) * mm, "end": v(1745.2, 1321.96) * mm});
            skArc(sketch, "E280", {"start": v(1745.2, 1321.96) * mm, "mid": v(1694.65, 1331.04) * mm, "end": v(1643.36, 1333.51) * mm});
            skArc(sketch, "E281", {"start": v(1643.36, 1333.51) * mm, "mid": v(1617.86, 1332.55) * mm, "end": v(1592.43, 1330.52) * mm});
            skArc(sketch, "E282", {"start": v(1592.43, 1330.52) * mm, "mid": v(1564.08, 1327.22) * mm, "end": v(1535.84, 1323.07) * mm});
            skArc(sketch, "E283", {"start": v(1535.84, 1323.07) * mm, "mid": v(1508.97, 1318.28) * mm, "end": v(1482.26, 1312.68) * mm});
            skArc(sketch, "E284", {"start": v(1482.26, 1312.68) * mm, "mid": v(1461.55, 1307.31) * mm, "end": v(1441.23, 1300.67) * mm});
            skSolve(sketch);
        }
        {
            var Q0;
            Q0=makeQuery(id+"F2.imprint","IMPRINT",FACE,{"disambiguationData":[TD([[makeQuery(id+"F2.imprint","IMPRINT",EDGE,{"derivedFrom":sQuery(id+"F2.wireOp",EDGE,"E1")}),-1.0]])]});
            var Q1;
            Q1=makeQuery(id+"F2.imprint","IMPRINT",FACE,{"disambiguationData":[TD([[makeQuery(id+"F2.imprint","IMPRINT",EDGE,{"derivedFrom":sQuery(id+"F2.wireOp",EDGE,"E143")}),-1.0]])]});
            extrude(context, id + "F3", {"entities" : qUnion([Q0, Q1]), "operationType" : NewBodyOperationType.REMOVE, "oppositeDirection" : true, "depth" : 508 * mm});
        }
    });
